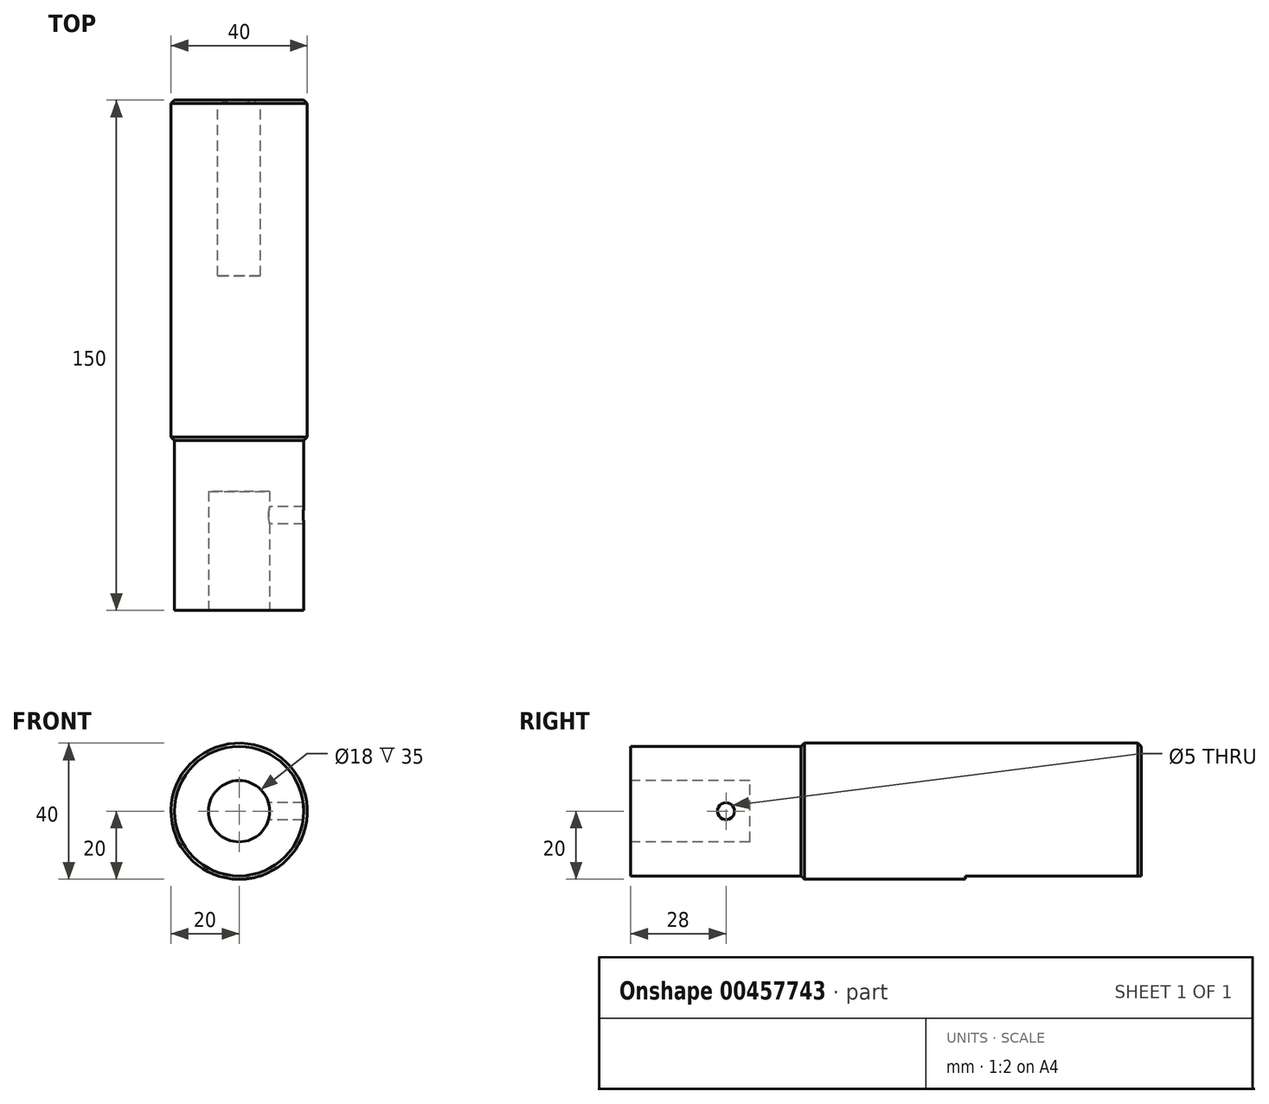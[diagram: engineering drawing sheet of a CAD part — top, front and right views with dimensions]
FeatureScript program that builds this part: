
annotation { "Feature Type Name" : "Feature", "Feature Type Description" : "" }
export const myFeature = defineFeature(function(context is Context, id is Id, definition is map)
    precondition{}
    {
        {
            var Q0;
            Q0=qCreatedBy(makeId("Front.planeOp"),FACE);
            var sketch = newSketch(context, id + "F0", { "sketchPlane" : qUnion([Q0])});
            skCircle(sketch, "E0", {"center": v(0, 0) * mm, "radius": 20 * mm});
            skSolve(sketch);
        }
        {
            var Q0;
            Q0 = qSketchRegion(id + "F0", true);
            extrude(context, id + "F1", {"entities" : qUnion([Q0]), "depth" : 150 * mm});
        }
        {
            var Q0;
            Q0=makeQuery(id+"F1.opExtrude","CAP_FACE",FACE,{"disambiguationData":[OSD([sQuery(id+"F0.wireOp",EDGE,"E0")])],"isStart":false});
            var sketch = newSketch(context, id + "F2", { "sketchPlane" : qUnion([Q0])});
            skCircle(sketch, "E1", {"center": v(0, 0) * mm, "radius": 9 * mm});
            skSolve(sketch);
        }
        {
            var Q0;
            Q0 = qSketchRegion(id + "F2", true);
            extrude(context, id + "F3", {"entities" : qUnion([Q0]), "operationType" : NewBodyOperationType.REMOVE, "oppositeDirection" : true, "depth" : 35 * mm});
        }
        {
            var Q0;
            Q0=qCreatedBy(makeId("Right.planeOp"),FACE);
            var sketch = newSketch(context, id + "F4", { "sketchPlane" : qUnion([Q0])});
            skPoint(sketch, "E2", {"position": v(-122, 0) * mm});
            skSolve(sketch);
        }
        {
            var Q0;
            Q0=sQuery(id+"F4.wireOp",VERTEX,"E2");
            var Q1;
            Q1=makeQuery(id+"F1.opExtrude","SWEPT_BODY",BODY,{"disambiguationData":[OSD([sQuery(id+"F0.wireOp",EDGE,"E0")])]});
            hole(context, id + "F5", {"style" : HoleStyle.SIMPLE, "endStyle" : HoleEndStyle.THROUGH, "oppositeDirection" : true, "holeDiameter" : 5 * mm, "isTappedThrough" : true, "tappedDepth" : 12 * mm, "tapClearance" : 3, "locations" : qUnion([Q0]), "scope" : qUnion([Q1])});
        }
        {
            var Q0;
            Q0=qCreatedBy(makeId("Top.planeOp"),FACE);
            cPlane(context, id + "F6", {"entities" : qUnion([Q0]), "cplaneType" : CPlaneType.OFFSET, "offset" : 20 * mm, "oppositeDirection" : true, "width" : 150 * mm, "height" : 150 * mm});
        }
        {
            var Q0;
            Q0=makeQuery(id+"F1.opExtrude","CAP_EDGE",EDGE,{"disambiguationData":[OSD([sQuery(id+"F0.wireOp",EDGE,"E0")])],"isStart":true});
            chamfer(context, id + "F7", {"entities" : qUnion([Q0]), "width" : 1 * mm, "tangentPropagation" : true});
        }
        {
            var Q0;
            Q0=makeQuery(id+"F1.opExtrude","CAP_FACE",FACE,{"disambiguationData":[OSD([sQuery(id+"F0.wireOp",EDGE,"E0")])],"isStart":false});
            var sketch = newSketch(context, id + "F8", { "sketchPlane" : qUnion([Q0])});
            skCircle(sketch, "E3", {"center": v(0, 0) * mm, "radius": 19 * mm});
            skCircle(sketch, "E4", {"center": v(0, 0) * mm, "radius": 22.02 * mm});
            skSolve(sketch);
        }
        {
            var Q0;
            Q0=qCreatedBy(id+"F6.planeOp",FACE);
            var sketch = newSketch(context, id + "F9", { "sketchPlane" : qUnion([Q0])});
            skLineSegment(sketch, "E5.bottom", {"start": v(18.01, -51.71) * mm, "end": v(-18.01, -51.71) * mm});
            skLineSegment(sketch, "E5.top", {"start": v(18.01, 51.71) * mm, "end": v(-18.01, 51.71) * mm});
            skLineSegment(sketch, "E5.left", {"start": v(18.01, -51.71) * mm, "end": v(18.01, 51.71) * mm});
            skLineSegment(sketch, "E5.right", {"start": v(-18.01, -51.71) * mm, "end": v(-18.01, 51.71) * mm});
            skPoint(sketch, "E5.middle", {"position": v(0, 0) * mm});
            skSolve(sketch);
        }
        {
            var Q0;
            Q0 = qSketchRegion(id + "F9", true);
            extrude(context, id + "F10", {"entities" : qUnion([Q0]), "operationType" : NewBodyOperationType.REMOVE, "depth" : 1 * mm});
        }
        {
            var Q0;
            Q0=makeQuery(id+"F8.imprint","IMPRINT",FACE,{"disambiguationData":[TD([[makeQuery(id+"F8.imprint","IMPRINT",EDGE,{"derivedFrom":sQuery(id+"F8.wireOp",EDGE,"E4")}),1.0]])]});
            extrude(context, id + "F11", {"entities" : qUnion([Q0]), "operationType" : NewBodyOperationType.REMOVE, "oppositeDirection" : true, "depth" : 25 * mm});
        }
        {
            var Q0;
            Q0 = qSketchRegion(id + "F8", true);
            extrude(context, id + "F12", {"entities" : qUnion([Q0]), "operationType" : NewBodyOperationType.REMOVE, "oppositeDirection" : true, "depth" : 50 * mm});
        }
        {
            var Q0;
            Q0=makeQuery(id+"F12.boolean.opBoolean","COPY",EDGE,{"derivedFrom":makeQuery(id+"F12.opExtrude","CAP_EDGE",EDGE,{"disambiguationData":[OSD([sQuery(id+"F8.wireOp",EDGE,"E3")])],"isStart":true})});
            var Q1;
            Q1=makeQuery(id+"F12.boolean.opBoolean","INTERSECT",EDGE,{"derivedFrom":[makeQuery(id+"F1.opExtrude","SWEPT_FACE",FACE,{"disambiguationData":[OSD([sQuery(id+"F0.wireOp",EDGE,"E0")])]}),makeQuery(id+"F12.opExtrude","CAP_FACE",FACE,{"disambiguationData":[OSD([sQuery(id+"F8.wireOp",EDGE,"E3"),sQuery(id+"F8.wireOp",EDGE,"E4")])],"isStart":false})]});
            chamfer(context, id + "F13", {"entities" : qUnion([Q0, Q1]), "width" : 1 * mm, "tangentPropagation" : true});
        }
    });
